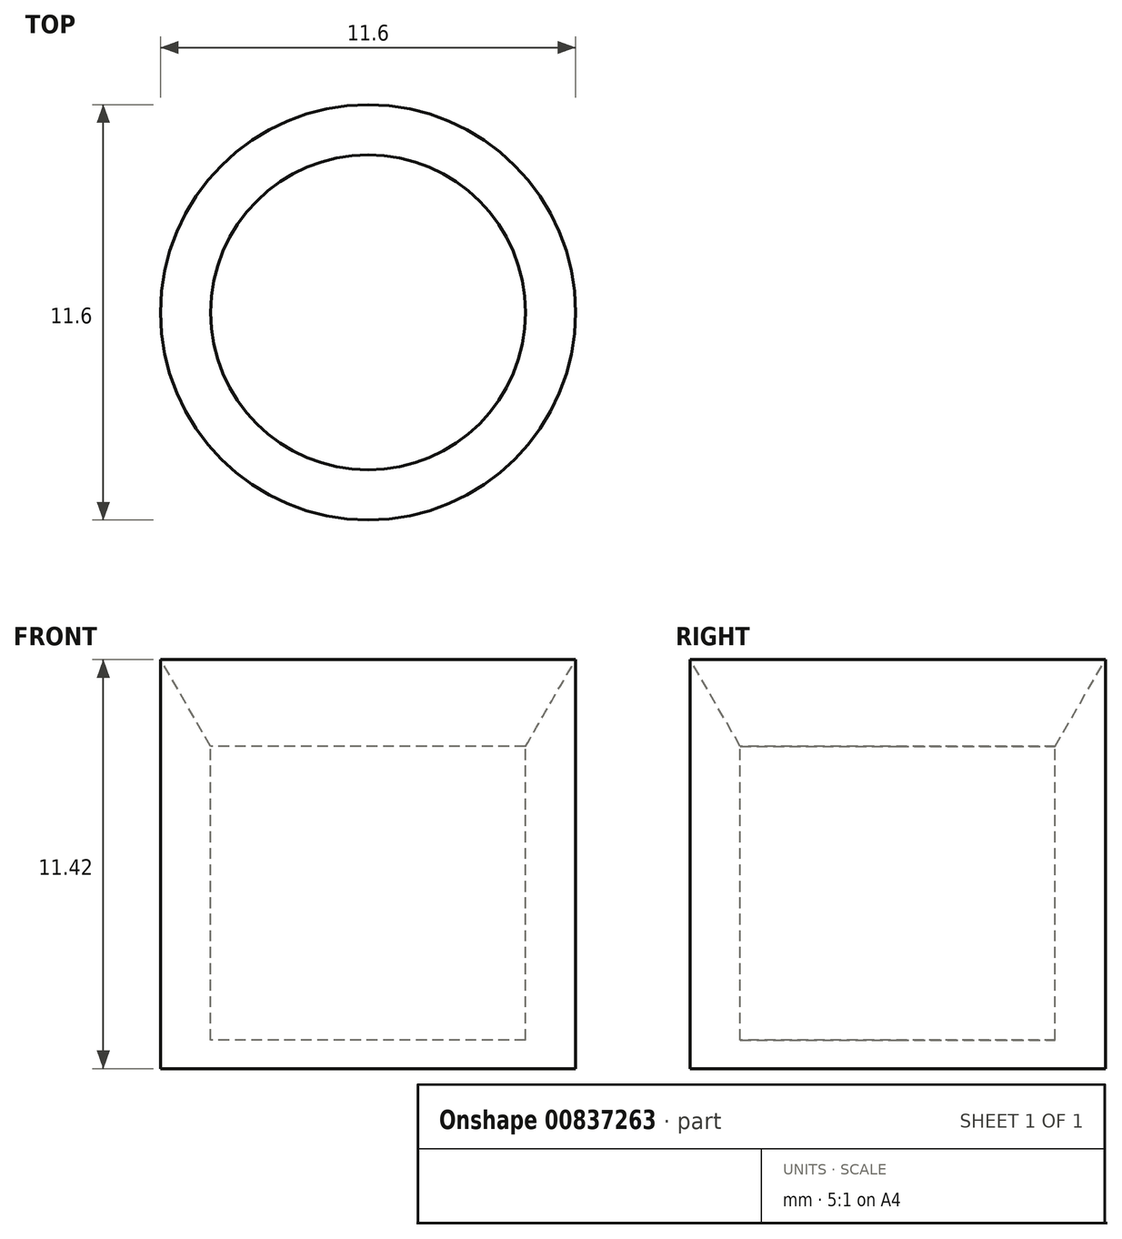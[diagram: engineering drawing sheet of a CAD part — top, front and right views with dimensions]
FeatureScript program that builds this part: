
annotation { "Feature Type Name" : "Feature", "Feature Type Description" : "" }
export const myFeature = defineFeature(function(context is Context, id is Id, definition is map)
    precondition{}
    {
        {
            var Q0;
            Q0=qCreatedBy(makeId("Front.planeOp"),FACE);
            var sketch = newSketch(context, id + "F0", { "sketchPlane" : qUnion([Q0])});
            skLineSegment(sketch, "E0", {"start": v(0, 36.01) * mm, "end": v(0, -34.93) * mm, "construction": true});
            skLineSegment(sketch, "E1", {"start": v(0, 0) * mm, "end": v(0, 9) * mm});
            skLineSegment(sketch, "E2", {"start": v(0, 0) * mm, "end": v(5.8, 0) * mm});
            skLineSegment(sketch, "E3", {"start": v(5.8, 0) * mm, "end": v(5.8, 11.42) * mm});
            skLineSegment(sketch, "E4", {"start": v(5.8, 11.42) * mm, "end": v(4.4, 9) * mm});
            skLineSegment(sketch, "E5", {"start": v(4.4, 9) * mm, "end": v(0, 9) * mm});
            skSolve(sketch);
        }
        {
            var Q0;
            Q0=makeQuery(id+"F0.imprint","IMPRINT",FACE,{"disambiguationData":[TD([[makeQuery(id+"F0.imprint","IMPRINT",EDGE,{"derivedFrom":sQuery(id+"F0.wireOp",EDGE,"E1")}),-1.0]])]});
            var Q1;
            Q1=sQuery(id+"F0.wireOp",EDGE,"E0");
            revolve(context, id + "F1", {"surfaceOperationType" : NewSurfaceOperationType.NEW, "entities" : qUnion([Q0]), "axis" : qUnion([Q1]), "revolveType" : RevolveType.FULL});
        }
        {
            var Q0;
            Q0=makeQuery(id+"F1.opRevolve","SWEPT_FACE",FACE,{"disambiguationData":[OSD([sQuery(id+"F0.wireOp",EDGE,"E5")])]});
            var sketch = newSketch(context, id + "F2", { "sketchPlane" : qUnion([Q0])});
            skCircle(sketch, "E6.0", {"center": v(0, 0) * mm, "radius": 4.4 * mm});
            skSolve(sketch);
        }
        {
            var Q0;
            Q0 = qSketchRegion(id + "F2", true);
            var Q1;
            Q1=makeQuery(id+"F1.opRevolve","SWEPT_FACE",FACE,{"disambiguationData":[OSD([sQuery(id+"F0.wireOp",EDGE,"E2")])]});
            extrude(context, id + "F3", {"entities" : qUnion([Q0]), "operationType" : NewBodyOperationType.REMOVE, "endBound" : BoundingType.UP_TO_SURFACE, "oppositeDirection" : true, "depth" : 25 * mm, "endBoundEntityFace" : qUnion([Q1]), "hasOffset" : true, "offsetDistance" : .8 * mm});
        }
    });
